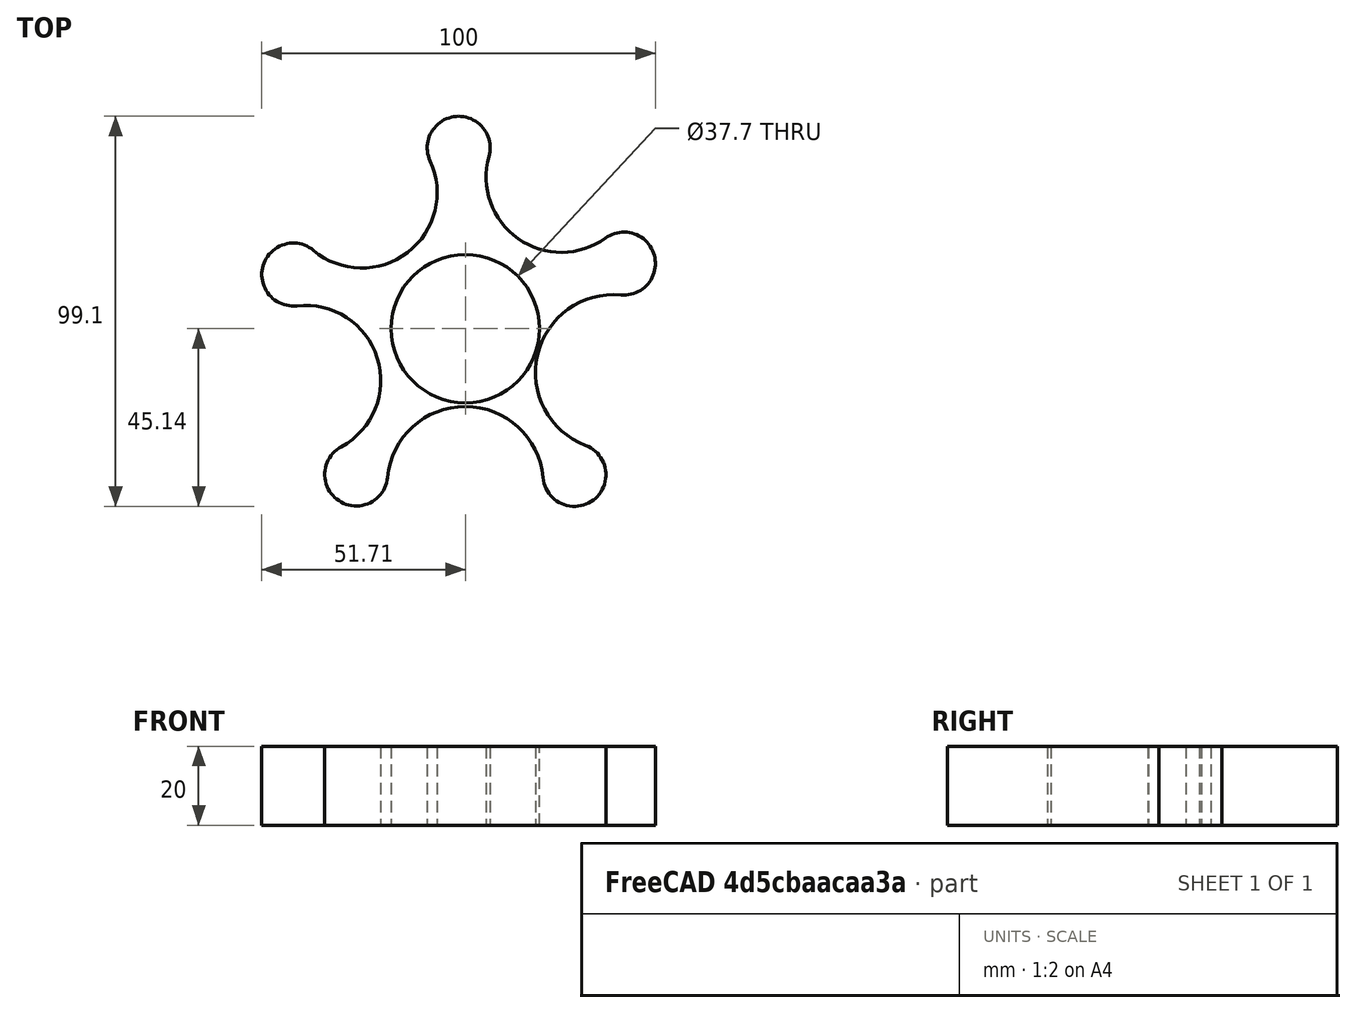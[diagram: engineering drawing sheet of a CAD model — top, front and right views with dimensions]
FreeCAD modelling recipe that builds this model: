
FCSTD DOCUMENT  (FreeCAD 0.16R5750 (Git))
Label: sketch-tutorial-better
License: CreativeCommons Attribution-NonCommercial-ShareAlike
LicenseURL: http://creativecommons.org/licenses/by-nc-sa/4.0/
objects: Sketcher::SketchObject×1, PartDesign::Pad×1
note: 3 computed .brp shape members not serialized (recipe doc carries the construction recipe); baked Part::Feature solids carry a one-line shape summary decoded from their .brp

FEATURE [Sketcher::SketchObject] Sketch
  sketch-geometry (16):
    g0: LineSegment [constr] StartX=0 StartY=0 StartZ=0 EndX=28.5317 EndY=9.27051 EndZ=0
    g1: LineSegment [constr] StartX=0 StartY=0 StartZ=0 EndX=17.6336 EndY=-24.2705 EndZ=0
    g2: LineSegment [constr] StartX=0 StartY=0 StartZ=0 EndX=-17.6336 EndY=-24.2705 EndZ=0
    g3: LineSegment [constr] StartX=0 StartY=0 StartZ=0 EndX=-28.5317 EndY=9.27051 EndZ=0
    g4: LineSegment [constr] StartX=0 StartY=0 StartZ=0 EndX=0 EndY=30 EndZ=0
    g5: Circle CenterX=0 CenterY=0 CenterZ=0 NormalX=0 NormalY=0 NormalZ=1 Radius=18.8499
    g6: ArcOfCircle CenterX=-1.68297 CenterY=45.9596 CenterZ=0 NormalX=0 NormalY=0 NormalZ=1 Radius=8 StartAngle=6.00515 EndAngle=9.85899
    g7: ArcOfCircle CenterX=40.295 CenterY=16.5429 CenterZ=0 NormalX=0 NormalY=0 NormalZ=1 Radius=8 StartAngle=4.61665 EndAngle=8.48033
    g8: ArcOfCircle CenterX=27.7146 CenterY=-37.1426 CenterZ=0 NormalX=0 NormalY=0 NormalZ=1 Radius=8 StartAngle=3.22907 EndAngle=7.48935
    g9: ArcOfCircle CenterX=-27.7045 CenterY=-37.03 CenterZ=0 NormalX=0 NormalY=0 NormalZ=1 Radius=8 StartAngle=2.06696 EndAngle=6.19165
    g10: ArcOfCircle CenterX=-43.7103 CenterY=13.765 CenterZ=0 NormalX=0 NormalY=0 NormalZ=1 Radius=8 StartAngle=0.873164 EndAngle=4.82674
    g11: ArcOfCircle CenterX=-26.2875 CenterY=34.5499 CenterZ=0 NormalX=0 NormalY=0 NormalZ=1 Radius=19.1213 StartAngle=4.01476 EndAngle=6.7174
    g12: ArcOfCircle CenterX=24.3968 CenterY=38.5158 CenterZ=0 NormalX=0 NormalY=0 NormalZ=1 Radius=19.1213 StartAngle=2.86356 EndAngle=5.33874
    g13: ArcOfCircle CenterX=0 CenterY=-39.5731 CenterZ=0 NormalX=0 NormalY=0 NormalZ=1 Radius=19.821 StartAngle=0.0874731 EndAngle=3.05005
    g14: ArcOfCircle CenterX=-40.6157 CenterY=-13.1791 CenterZ=0 NormalX=0 NormalY=0 NormalZ=1 Radius=19.1213 StartAngle=5.20855 EndAngle=7.96833
    g15: ArcOfCircle CenterX=37.6356 CenterY=-11.1507 CenterZ=0 NormalX=0 NormalY=0 NormalZ=1 Radius=19.821 StartAngle=1.47506 EndAngle=4.34776
  constraints (34):
    c: Coincident(g0,g-1)
    c: Coincident(g1,g-1)
    c: Coincident(g2,g-1)
    c: Coincident(g3,g-1)
    c: Coincident(g4,g-1)
    c: Coincident(g5,g-1)
    c: Equal(g0,g1)
    c: Equal(g1,g2)
    c: Equal(g2,g3)
    c: Equal(g3,g4)
    c: Equal(g6,g7)
    c: Equal(g7,g8)
    c: Equal(g8,g9)
    c: Equal(g9,g10)
    c: Equal(g14,g11)
    c: Equal(g11,g12)
    c: Angle(g0,g4) = 1.25664
    c: Angle(g4,g3) = 1.25664
    c: Angle(g3,g2) = 1.25664
    c: Angle(g2,g1) = 1.25664
    c: Tangent(g7,g12) = 1.5708
    c: Tangent(g12,g6) = 1.5708
    c: Tangent(g11,g6) = 1.5708
    c: Tangent(g11,g10) = 1.5708
    c: Tangent(g14,g10) = 1.5708
    c: Tangent(g14,g9) = 1.5708
    c: Tangent(g13,g9) = 1.5708
    c: Tangent(g13,g8) = 1.5708
    c: Equal(g15,g13)
    c: Tangent(g7,g15) = 1.5708
    c: Tangent(g8,g15) = 1.5708
    c: DistanceY(g4) = 30
    c: Radius(g6) = 8
    c: Vertical(g4)
FEATURE [PartDesign::Pad] Pad
  Length = 20
  Length2 = 100
  Sketch = -> Sketch
  Type = 0
